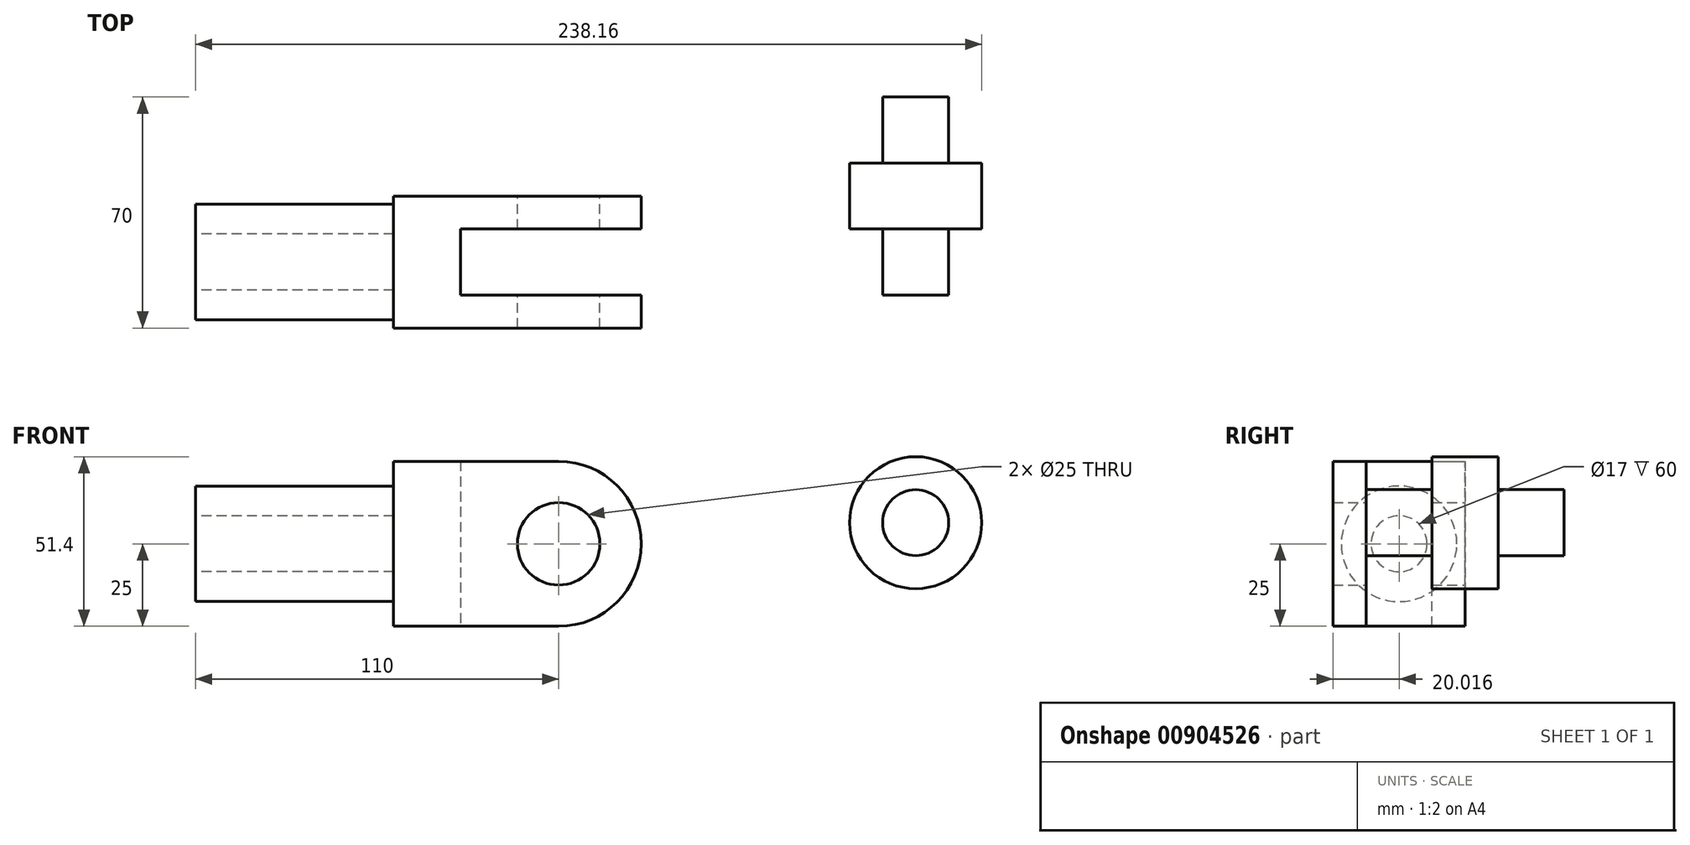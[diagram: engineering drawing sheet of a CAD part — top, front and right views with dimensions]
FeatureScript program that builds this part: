
annotation { "Feature Type Name" : "Feature", "Feature Type Description" : "" }
export const myFeature = defineFeature(function(context is Context, id is Id, definition is map)
    precondition{}
    {
        {
            var Q0;
            Q0=qCreatedBy(makeId("Front.planeOp"),FACE);
            var sketch = newSketch(context, id + "F0", { "sketchPlane" : qUnion([Q0])});
            skCircle(sketch, "E0", {"center": v(0, 0) * mm, "radius": 12.5 * mm});
            skArc(sketch, "E1", {"start": v(0, -25) * mm, "mid": v(25, 0) * mm, "end": v(0, 25) * mm});
            skLineSegment(sketch, "E2", {"start": v(0, 25) * mm, "end": v(-50, 25) * mm});
            skLineSegment(sketch, "E3", {"start": v(-50, 25) * mm, "end": v(-50, -25) * mm});
            skLineSegment(sketch, "E4", {"start": v(-50, -25) * mm, "end": v(0, -25) * mm});
            skSolve(sketch);
        }
        {
            var Q0;
            Q0=makeQuery(id+"F0.imprint","IMPRINT",FACE,{"disambiguationData":[TD([[makeQuery(id+"F0.imprint","IMPRINT",EDGE,{"derivedFrom":sQuery(id+"F0.wireOp",EDGE,"E0")}),-1.0]])]});
            extrude(context, id + "F1", {"entities" : qUnion([Q0]), "depth" : 10 * mm, "offsetDistance" : 25 * mm});
        }
        {
            var Q0;
            Q0=makeQuery(id+"F1.opExtrude","CAP_FACE",FACE,{"disambiguationData":[OSD([sQuery(id+"F0.wireOp",EDGE,"E0"),sQuery(id+"F0.wireOp",EDGE,"E1"),sQuery(id+"F0.wireOp",EDGE,"E2"),sQuery(id+"F0.wireOp",EDGE,"E3"),sQuery(id+"F0.wireOp",EDGE,"E4")])],"isStart":false});
            cPlane(context, id + "F2", {"entities" : qUnion([Q0]), "cplaneType" : CPlaneType.OFFSET, "offset" : 20 * mm, "width" : 150 * mm, "height" : 150 * mm});
        }
        {
            var Q0;
            Q0=qCreatedBy(id+"F2.planeOp",FACE);
            var sketch = newSketch(context, id + "F3", { "sketchPlane" : qUnion([Q0])});
            skLineSegment(sketch, "E5.0.0", {"start": v(-50, 25) * mm, "end": v(-50, -25) * mm});
            skLineSegment(sketch, "E5.0.1", {"start": v(-50, -25) * mm, "end": v(0, -25) * mm});
            skArc(sketch, "E5.0.2", {"start": v(0, -25) * mm, "mid": v(25, 0) * mm, "end": v(0, 25) * mm});
            skLineSegment(sketch, "E5.0.3", {"start": v(0, 25) * mm, "end": v(-50, 25) * mm});
            skCircle(sketch, "E6.0", {"center": v(0, 0) * mm, "radius": 12.5 * mm});
            skSolve(sketch);
        }
        {
            var Q0;
            Q0=makeQuery(id+"F3.imprint","IMPRINT",FACE,{"disambiguationData":[TD([[makeQuery(id+"F3.imprint","IMPRINT",EDGE,{"derivedFrom":sQuery(id+"F3.wireOp",EDGE,"E5.0.0")}),1.0]])]});
            extrude(context, id + "F4", {"entities" : qUnion([Q0]), "depth" : 10 * mm, "offsetDistance" : 25 * mm});
        }
        {
            var Q0;
            Q0=makeQuery(id+"F1.opExtrude","CAP_FACE",FACE,{"disambiguationData":[OSD([sQuery(id+"F0.wireOp",EDGE,"E0"),sQuery(id+"F0.wireOp",EDGE,"E1"),sQuery(id+"F0.wireOp",EDGE,"E2"),sQuery(id+"F0.wireOp",EDGE,"E3"),sQuery(id+"F0.wireOp",EDGE,"E4")])],"isStart":false});
            var sketch = newSketch(context, id + "F5", { "sketchPlane" : qUnion([Q0])});
            skLineSegment(sketch, "E7.bottom", {"start": v(-50, 25) * mm, "end": v(-29.7, 25) * mm});
            skLineSegment(sketch, "E7.top", {"start": v(-50, -25) * mm, "end": v(-29.7, -25) * mm});
            skLineSegment(sketch, "E7.left", {"start": v(-50, 25) * mm, "end": v(-50, -25) * mm});
            skLineSegment(sketch, "E7.right", {"start": v(-29.7, 25) * mm, "end": v(-29.7, -25) * mm});
            skSolve(sketch);
        }
        {
            var Q0;
            Q0=makeQuery(id+"F5.imprint","IMPRINT",FACE,{"disambiguationData":[TD([[makeQuery(id+"F5.imprint","IMPRINT",EDGE,{"derivedFrom":sQuery(id+"F5.wireOp",EDGE,"E7.bottom")}),1.0]])]});
            extrude(context, id + "F6", {"entities" : qUnion([Q0]), "operationType" : NewBodyOperationType.ADD, "endBound" : BoundingType.UP_TO_NEXT, "depth" : 25 * mm, "offsetDistance" : 25 * mm});
        }
        {
            var Q0;
            Q0=makeQuery(id+"F6.boolean.opBoolean","MERGE",FACE,{"derivedFrom":[makeQuery(id+"F1.opExtrude","SWEPT_FACE",FACE,{"disambiguationData":[OSD([sQuery(id+"F0.wireOp",EDGE,"E3")])]}),makeQuery(id+"F4.opExtrude","SWEPT_FACE",FACE,{"disambiguationData":[OSD([sQuery(id+"F3.wireOp",EDGE,"E5.0.0")])]}),makeQuery(id+"F6.opExtrude","SWEPT_FACE",FACE,{"disambiguationData":[OSD([sQuery(id+"F5.wireOp",EDGE,"E7.left")])]})]});
            var sketch = newSketch(context, id + "F7", { "sketchPlane" : qUnion([Q0])});
            skCircle(sketch, "E8", {"center": v(19.98, 0) * mm, "radius": 17.5 * mm});
            skSolve(sketch);
        }
        {
            var Q0;
            Q0=makeQuery(id+"F7.imprint","IMPRINT",FACE,{"disambiguationData":[TD([[makeQuery(id+"F7.imprint","IMPRINT",EDGE,{"derivedFrom":sQuery(id+"F7.wireOp",EDGE,"E8")}),1.0]])]});
            extrude(context, id + "F8", {"entities" : qUnion([Q0]), "operationType" : NewBodyOperationType.ADD, "depth" : 60 * mm, "offsetDistance" : 25 * mm});
        }
        {
            var Q0;
            Q0=makeQuery(id+"F8.opExtrude","CAP_FACE",FACE,{"disambiguationData":[OSD([sQuery(id+"F7.wireOp",EDGE,"E8")])],"isStart":false});
            var sketch = newSketch(context, id + "F9", { "sketchPlane" : qUnion([Q0])});
            skCircle(sketch, "E9", {"center": v(19.98, 0) * mm, "radius": 8.5 * mm});
            skSolve(sketch);
        }
        {
            var Q0;
            Q0=makeQuery(id+"F9.imprint","IMPRINT",FACE,{"disambiguationData":[TD([[makeQuery(id+"F9.imprint","IMPRINT",EDGE,{"derivedFrom":sQuery(id+"F9.wireOp",EDGE,"E9")}),1.0]])]});
            extrude(context, id + "F10", {"entities" : qUnion([Q0]), "operationType" : NewBodyOperationType.REMOVE, "oppositeDirection" : true, "depth" : 60 * mm, "offsetDistance" : 25 * mm});
        }
        {
            var Q0;
            Q0=qCreatedBy(makeId("Front.planeOp"),FACE);
            var sketch = newSketch(context, id + "F11", { "sketchPlane" : qUnion([Q0])});
            skCircle(sketch, "E10", {"center": v(108.16, 6.4) * mm, "radius": 20 * mm});
            skSolve(sketch);
        }
        {
            var Q0;
            Q0=makeQuery(id+"F11.imprint","IMPRINT",FACE,{"disambiguationData":[TD([[makeQuery(id+"F11.imprint","IMPRINT",EDGE,{"derivedFrom":sQuery(id+"F11.wireOp",EDGE,"E10")}),1.0]])]});
            extrude(context, id + "F12", {"entities" : qUnion([Q0]), "depth" : 10 * mm, "offsetDistance" : 25 * mm, "hasSecondDirection" : true, "secondDirectionOppositeDirection" : true, "secondDirectionDepth" : 10 * mm});
        }
        {
            var Q0;
            Q0=makeQuery(id+"F12.opExtrude","CAP_FACE",FACE,{"disambiguationData":[OSD([sQuery(id+"F11.wireOp",EDGE,"E10")])],"isStart":false});
            var sketch = newSketch(context, id + "F13", { "sketchPlane" : qUnion([Q0])});
            skCircle(sketch, "E11", {"center": v(108.16, 6.4) * mm, "radius": 10 * mm});
            skSolve(sketch);
        }
        {
            var Q0;
            Q0=makeQuery(id+"F13.imprint","IMPRINT",FACE,{"disambiguationData":[TD([[makeQuery(id+"F13.imprint","IMPRINT",EDGE,{"derivedFrom":sQuery(id+"F13.wireOp",EDGE,"E11")}),1.0]])]});
            extrude(context, id + "F14", {"entities" : qUnion([Q0]), "operationType" : NewBodyOperationType.ADD, "depth" : 20 * mm, "offsetDistance" : 25 * mm});
        }
        {
            var Q0;
            Q0=makeQuery(id+"F12.opExtrude","CAP_FACE",FACE,{"disambiguationData":[OSD([sQuery(id+"F11.wireOp",EDGE,"E10")])],"isStart":true});
            var sketch = newSketch(context, id + "F15", { "sketchPlane" : qUnion([Q0])});
            skCircle(sketch, "E12", {"center": v(-108.16, 6.4) * mm, "radius": 10 * mm});
            skSolve(sketch);
        }
        {
            var Q0;
            Q0=makeQuery(id+"F15.imprint","IMPRINT",FACE,{"disambiguationData":[TD([[makeQuery(id+"F15.imprint","IMPRINT",EDGE,{"derivedFrom":sQuery(id+"F15.wireOp",EDGE,"E12")}),1.0]])]});
            extrude(context, id + "F16", {"entities" : qUnion([Q0]), "operationType" : NewBodyOperationType.ADD, "depth" : 20 * mm, "offsetDistance" : 25 * mm});
        }
    });
